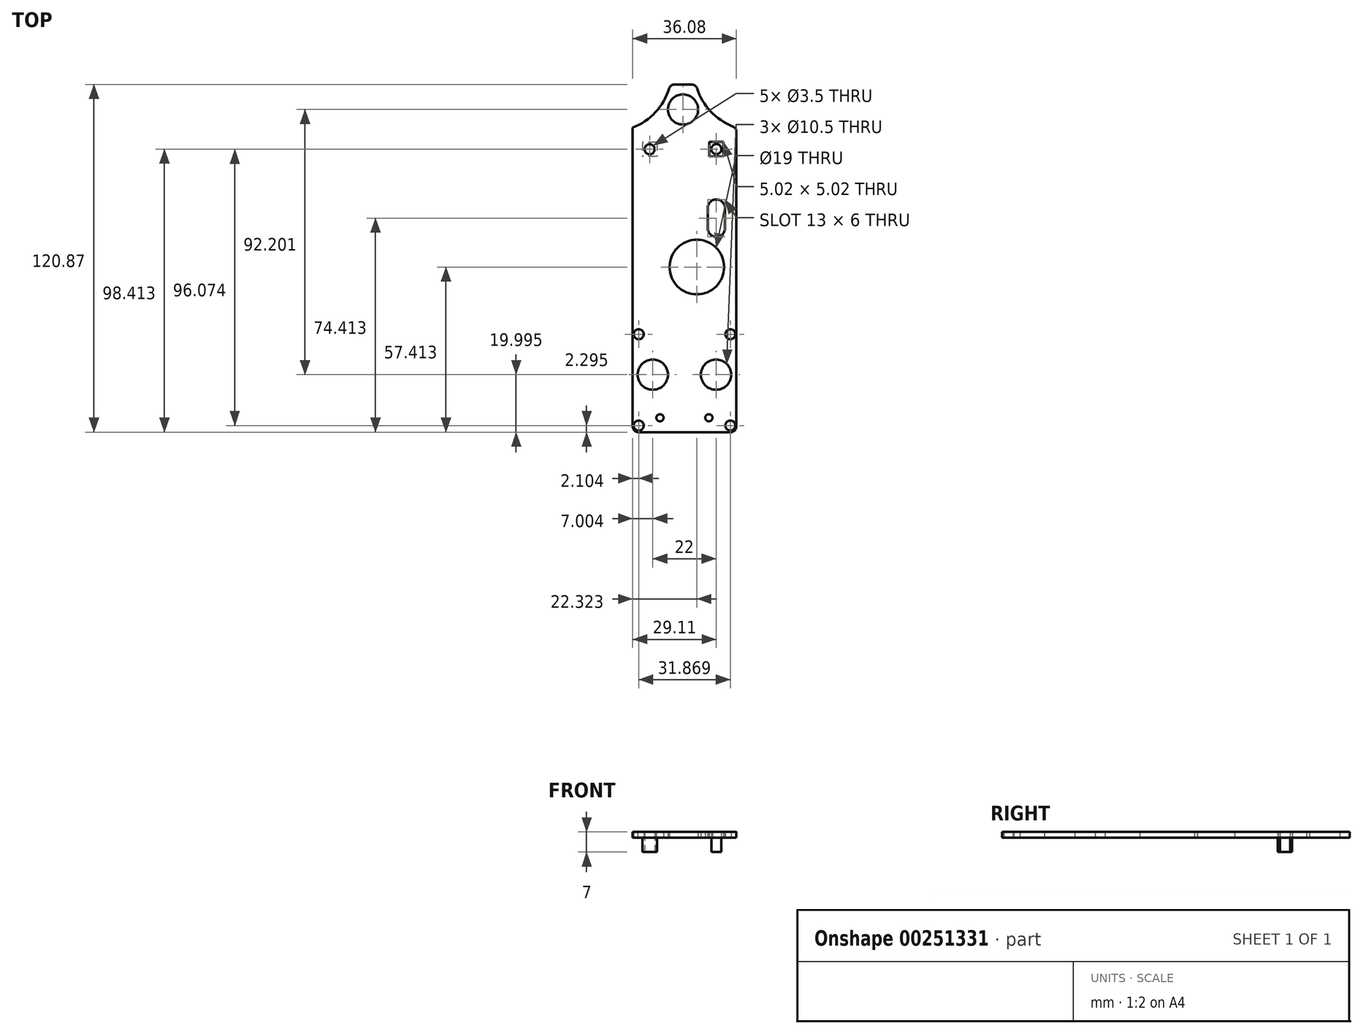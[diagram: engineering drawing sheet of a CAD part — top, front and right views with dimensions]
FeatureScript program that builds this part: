
annotation { "Feature Type Name" : "Feature", "Feature Type Description" : "" }
export const myFeature = defineFeature(function(context is Context, id is Id, definition is map)
    precondition{}
    {
        {
            var Q0;
            Q0=qCreatedBy(makeId("Top.planeOp"),FACE);
            var sketch = newSketch(context, id + "F0", { "sketchPlane" : qUnion([Q0])});
            skLineSegment(sketch, "E0.right", {"start": v(-28.8, -14.78) * mm, "end": v(-28.8, 65.22) * mm});
            skPoint(sketch, "E1.centerSnap0", {"position": v(-25.72, 59.72) * mm});
            skLineSegment(sketch, "E2.left", {"start": v(-28.8, -14.78) * mm, "end": v(-28.8, -16.57) * mm});
            skLineSegment(sketch, "E3", {"start": v(-11.3, 57.54) * mm, "end": v(-11.13, -24.08) * mm, "construction": true});
            skCircle(sketch, "E4", {"center": v(-22.9, 57.72) * mm, "radius": 1.75 * mm});
            skCircle(sketch, "E5.MirrorC", {"center": v(0.3, 57.76) * mm, "radius": 1.75 * mm});
            skLineSegment(sketch, "E6", {"start": v(-28.8, 65.22) * mm, "end": v(5.2, 65.22) * mm});
            skLineSegment(sketch, "E7", {"start": v(7.27, -16.57) * mm, "end": v(7.28, 65.22) * mm});
            skLineSegment(sketch, "E8", {"start": v(7.28, 65.22) * mm, "end": v(-28.8, 65.22) * mm});
            skLineSegment(sketch, "E9", {"start": v(7.27, -16.57) * mm, "end": v(7.27, -40.65) * mm});
            skLineSegment(sketch, "E10", {"start": v(7.27, -40.65) * mm, "end": v(-28.8, -40.66) * mm});
            skLineSegment(sketch, "E11", {"start": v(-28.8, -40.66) * mm, "end": v(-28.8, -16.57) * mm});
            skCircle(sketch, "E12", {"center": v(-26.7, -38.35) * mm, "radius": 1.75 * mm});
            skCircle(sketch, "E13", {"center": v(5.17, -38.35) * mm, "radius": 1.75 * mm});
            skCircle(sketch, "E14", {"center": v(-26.7, -6.6) * mm, "radius": 1.75 * mm});
            skCircle(sketch, "E15", {"center": v(5.17, -6.6) * mm, "radius": 1.75 * mm});
            skLineSegment(sketch, "E16.bottom", {"start": v(-20.4, 60.22) * mm, "end": v(-25.4, 60.22) * mm});
            skLineSegment(sketch, "E16.top", {"start": v(-20.4, 55.22) * mm, "end": v(-25.4, 55.22) * mm});
            skLineSegment(sketch, "E16.left", {"start": v(-20.4, 60.22) * mm, "end": v(-20.4, 55.22) * mm});
            skLineSegment(sketch, "E16.right", {"start": v(-25.4, 60.22) * mm, "end": v(-25.4, 55.22) * mm});
            skLineSegment(sketch, "E17.MirrorCS", {"start": v(-2.2, 60.25) * mm, "end": v(-2.18, 55.25) * mm});
            skLineSegment(sketch, "E18.MirrorCS", {"start": v(-2.18, 55.25) * mm, "end": v(2.82, 55.27) * mm});
            skLineSegment(sketch, "E19.MirrorCS", {"start": v(2.8, 60.27) * mm, "end": v(2.82, 55.27) * mm});
            skLineSegment(sketch, "E20.MirrorCS", {"start": v(-2.2, 60.25) * mm, "end": v(2.8, 60.27) * mm});
            skCircle(sketch, "E21", {"center": v(0.3, 37.26) * mm, "radius": 3 * mm});
            skCircle(sketch, "E22", {"center": v(0.3, 30.26) * mm, "radius": 3 * mm});
            skLineSegment(sketch, "E23", {"start": v(3.3, 37.26) * mm, "end": v(3.3, 30.26) * mm});
            skLineSegment(sketch, "E24", {"start": v(-2.7, 37.26) * mm, "end": v(-2.7, 30.26) * mm});
            skCircle(sketch, "E25", {"center": v(-6.48, 16.76) * mm, "radius": 9.5 * mm});
            skLineSegment(sketch, "E26", {"start": v(-15.8, 80.22) * mm, "end": v(-6.8, 80.22) * mm});
            skArc(sketch, "E27", {"start": v(-28.8, 65.22) * mm, "mid": v(-20.43, 71.1) * mm, "end": v(-15.8, 80.22) * mm});
            skArc(sketch, "E28", {"start": v(-6.8, 80.22) * mm, "mid": v(-1.7, 70.9) * mm, "end": v(7.28, 65.22) * mm});
            skCircle(sketch, "E29", {"center": v(-11.3, 71.55) * mm, "radius": 5.25 * mm});
            skPoint(sketch, "E29.centerSnap0", {"position": v(-11.3, 80.22) * mm});
            skCircle(sketch, "E30", {"center": v(-21.8, -20.66) * mm, "radius": 5.25 * mm});
            skCircle(sketch, "E31", {"center": v(0.2, -20.66) * mm, "radius": 5.25 * mm});
            skCircle(sketch, "E32", {"center": v(-19.3, -35.66) * mm, "radius": 1.25 * mm});
            skCircle(sketch, "E33", {"center": v(-2.3, -35.66) * mm, "radius": 1.25 * mm});
            skSolve(sketch);
        }
        {
            var Q0;
            {var subQ0=sQuery(id+"F0.wireOp",EDGE,"E0.right");Q0=makeQuery(id+"F0.imprint","IMPRINT",FACE,{"disambiguationData":[TD([[makeQuery(id+"F0.imprint","IMPRINT",EDGE,{"derivedFrom":subQ0}),-1.0]])]});}
            var Q1;
            Q1=makeQuery(id+"F0.imprint","IMPRINT",FACE,{"disambiguationData":[TD([[makeQuery(id+"F0.imprint","IMPRINT",EDGE,{"derivedFrom":sQuery(id+"F0.wireOp",EDGE,"E4")}),-1.0]])]});
            var Q2;
            Q2=makeQuery(id+"F0.imprint","IMPRINT",FACE,{"disambiguationData":[TD([[makeQuery(id+"F0.imprint","IMPRINT",EDGE,{"derivedFrom":sQuery(id+"F0.wireOp",EDGE,"E5.MirrorC")}),1.0]])]});
            var Q3;
            Q3=makeQuery(id+"F0.imprint","IMPRINT",FACE,{"disambiguationData":[TD([[makeQuery(id+"F0.imprint","IMPRINT",EDGE,{"derivedFrom":sQuery(id+"F0.wireOp",EDGE,"E26")}),-1.0]])]});
            extrude(context, id + "F1", {"entities" : qUnion([Q0, Q1, Q2, Q3]), "depth" : 2 * mm});
        }
        {
            var Q0;
            Q0=makeQuery(id+"F0.imprint","IMPRINT",FACE,{"disambiguationData":[TD([[makeQuery(id+"F0.imprint","IMPRINT",EDGE,{"derivedFrom":sQuery(id+"F0.wireOp",EDGE,"E5.MirrorC")}),1.0]])]});
            var Q1;
            Q1=makeQuery(id+"F0.imprint","IMPRINT",FACE,{"disambiguationData":[TD([[makeQuery(id+"F0.imprint","IMPRINT",EDGE,{"derivedFrom":sQuery(id+"F0.wireOp",EDGE,"E4")}),-1.0]])]});
            extrude(context, id + "F2", {"entities" : qUnion([Q0, Q1]), "operationType" : NewBodyOperationType.ADD, "oppositeDirection" : true, "depth" : 5 * mm});
        }
        {
            var Q0;
            Q0=makeQuery(id+"F1.opExtrude","SWEPT_EDGE",EDGE,{"disambiguationData":[OSD([sQuery(id+"F0.wireOp",EDGE,"E0.right"),sQuery(id+"F0.wireOp",EDGE,"E8")])]});
            var Q1;
            Q1=makeQuery(id+"F1.opExtrude","SWEPT_EDGE",EDGE,{"disambiguationData":[OSD([sQuery(id+"F0.wireOp",EDGE,"E7"),sQuery(id+"F0.wireOp",EDGE,"E8")])]});
            var Q2;
            Q2=makeQuery(id+"F1.opExtrude","SWEPT_EDGE",EDGE,{"disambiguationData":[OSD([sQuery(id+"F0.wireOp",EDGE,"E9"),sQuery(id+"F0.wireOp",EDGE,"E10")])]});
            var Q3;
            Q3=makeQuery(id+"F1.opExtrude","SWEPT_EDGE",EDGE,{"disambiguationData":[OSD([sQuery(id+"F0.wireOp",EDGE,"E10"),sQuery(id+"F0.wireOp",EDGE,"E11")])]});
            var Q4;
            Q4=makeQuery(id+"F1.opExtrude","SWEPT_EDGE",EDGE,{"disambiguationData":[OSD([sQuery(id+"F0.wireOp",EDGE,"E26"),sQuery(id+"F0.wireOp",EDGE,"E27")])]});
            var Q5;
            Q5=makeQuery(id+"F1.opExtrude","SWEPT_EDGE",EDGE,{"disambiguationData":[OSD([sQuery(id+"F0.wireOp",EDGE,"E26"),sQuery(id+"F0.wireOp",EDGE,"E28")])]});
            fillet(context, id + "F3", {"entities" : qUnion([Q0, Q1, Q2, Q3, Q4, Q5]), "radius" : 2 * mm, "tangentPropagation" : true, "allowEdgeOverflow" : false});
        }
    });
